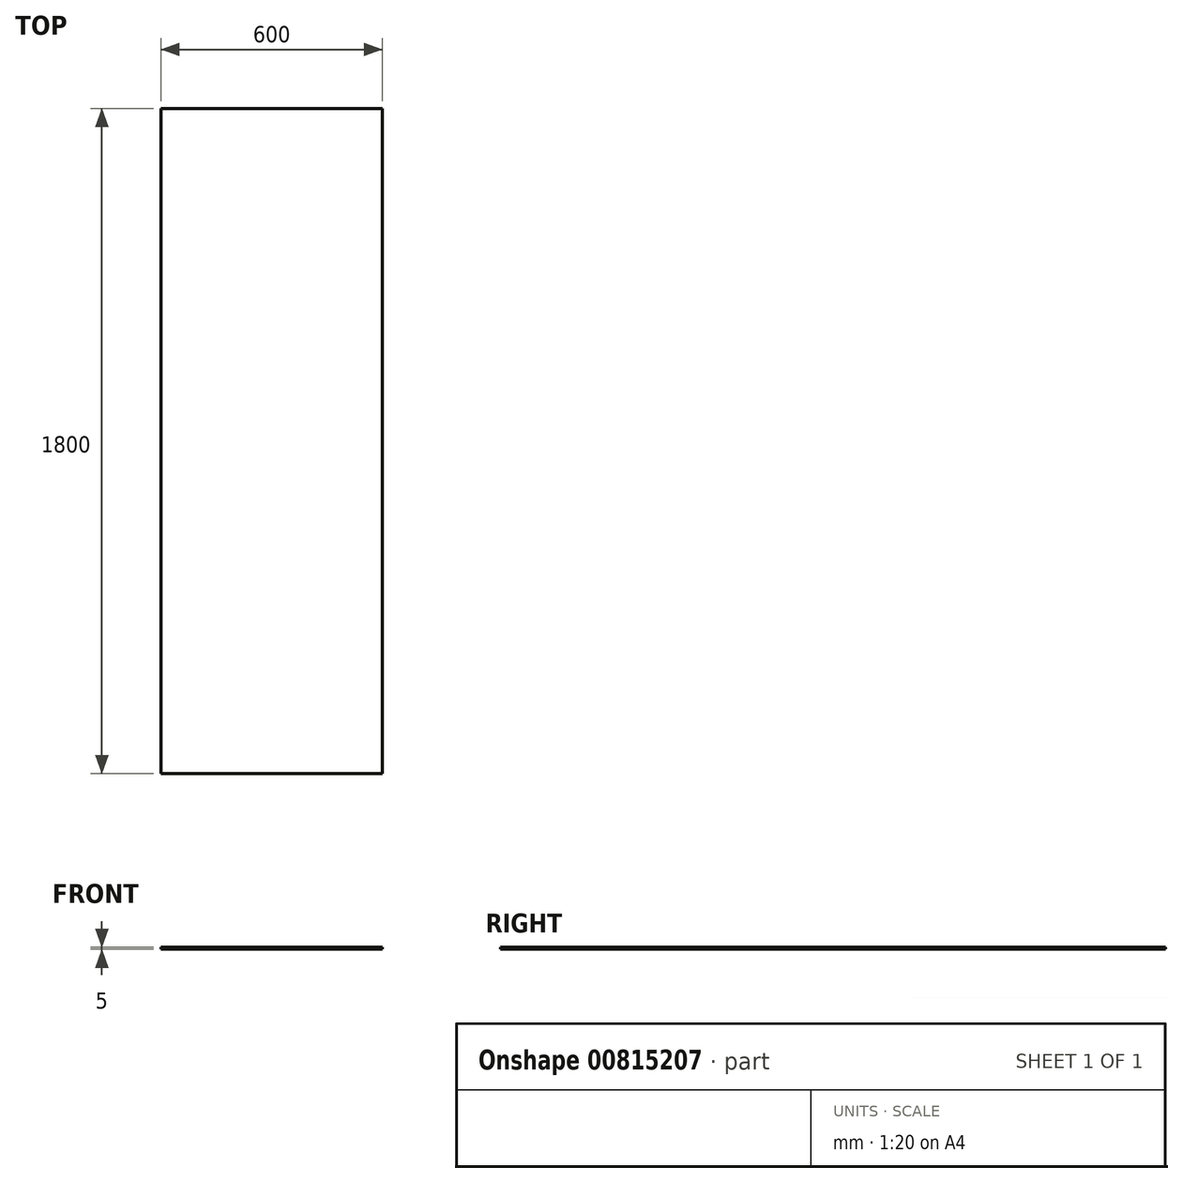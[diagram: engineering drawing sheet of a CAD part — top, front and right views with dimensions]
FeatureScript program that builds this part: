
annotation { "Feature Type Name" : "Feature", "Feature Type Description" : "" }
export const myFeature = defineFeature(function(context is Context, id is Id, definition is map)
    precondition{}
    {
        {
            var Q0;
            Q0=qCreatedBy(makeId("Front.planeOp"),FACE);
            var sketch = newSketch(context, id + "F0", { "sketchPlane" : qUnion([Q0])});
            skLineSegment(sketch, "E0", {"start": v(-240.15, -8.63) * mm, "end": v(-240.15, -3.63) * mm});
            skLineSegment(sketch, "E1", {"start": v(-240.15, -3.63) * mm, "end": v(359.85, -3.63) * mm});
            skLineSegment(sketch, "E2", {"start": v(359.85, -3.63) * mm, "end": v(359.85, -8.63) * mm});
            skLineSegment(sketch, "E3", {"start": v(359.85, -8.63) * mm, "end": v(-240.15, -8.63) * mm});
            skSolve(sketch);
        }
        {
            var Q0;
            Q0 = qSketchRegion(id + "F0", true);
            extrude(context, id + "F1", {"entities" : qUnion([Q0]), "oppositeDirection" : true, "depth" : 1800 * mm, "offsetDistance" : 25 * mm});
        }
    });
